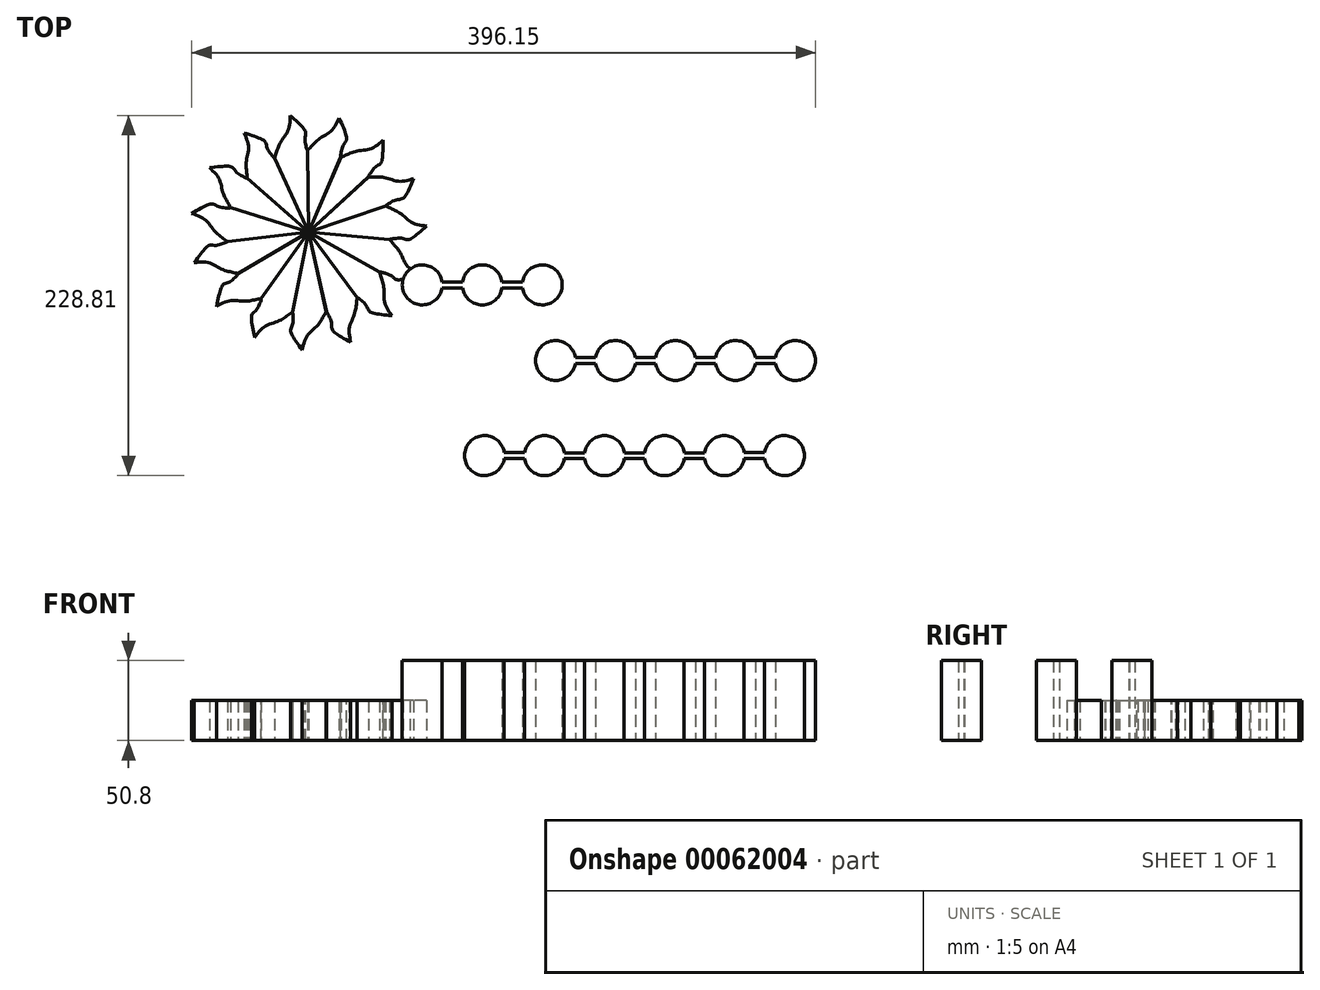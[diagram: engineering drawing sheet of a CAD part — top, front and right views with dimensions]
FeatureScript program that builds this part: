
annotation { "Feature Type Name" : "Feature", "Feature Type Description" : "" }
export const myFeature = defineFeature(function(context is Context, id is Id, definition is map)
    precondition{}
    {
        {
            var Q0;
            Q0=qCreatedBy(makeId("Top.planeOp"),FACE);
            var sketch = newSketch(context, id + "F0", { "sketchPlane" : qUnion([Q0])});
            skCircle(sketch, "E0", {"center": v(-72.3, 33.55) * mm, "radius": 46.86 * mm, "construction": true});
            skPoint(sketch, "E1", {"position": v(-84, 107.69) * mm});
            skPoint(sketch, "E2", {"position": v(-52.55, 106.29) * mm});
            skFitSpline(sketch, "E3", {"points": [v(-84, 107.69) * mm, v(-85.17, 98.25) * mm, v(-89.63, 91.3) * mm, v(-92.12, 85.8) * mm, v(-93.88, 80.61) * mm], "startDerivative": vector(-0.18, -34.68) * mm, "endDerivative": vector(-7.94, -23.8) * mm});
            skFitSpline(sketch, "E4", {"points": [v(-84, 107.69) * mm, v(-76.24, 100.43) * mm, v(-74.06, 96.7) * mm, v(-74.58, 92.65) * mm, v(-73.75, 87.67) * mm, v(-72.87, 85.38) * mm], "startDerivative": vector(30.23, -26.75) * mm, "endDerivative": vector(11.37, -13.18) * mm});
            skLineSegment(sketch, "E5", {"start": v(-93.88, 80.61) * mm, "end": v(-72.3, 33.55) * mm});
            skLineSegment(sketch, "E6", {"start": v(-72.87, 85.38) * mm, "end": v(-72.3, 33.55) * mm});
            skFitSpline(sketch, "E7", {"points": [v(64.47, 13.1) * mm, v(67.63, 14.05) * mm, v(71.16, 16.5) * mm, v(74.15, 19.89) * mm, v(77.5, 21.96) * mm, v(81.01, 21.97) * mm, v(84.14, 19.15) * mm, v(86.86, 16.13) * mm, v(90.86, 13.32) * mm, v(96.34, 13.11) * mm, v(100.52, 15.65) * mm, v(104.5, 20.68) * mm, v(107.3, 22) * mm, v(110.25, 22) * mm, v(114.68, 20.13) * mm, v(117.22, 16.95) * mm, v(119.43, 14.56) * mm, v(123.54, 13.1) * mm, v(127.31, 13.48) * mm, v(130.94, 16.58) * mm, v(133.75, 20.53) * mm, v(137.67, 22.62) * mm, v(142.59, 22.5) * mm, v(146.88, 19.99) * mm, v(149.63, 15.48) * mm, v(152.68, 13.12) * mm, v(156.88, 14.14) * mm, v(159.57, 16.3) * mm, v(162.65, 19.41) * mm, v(165.82, 22.33) * mm, v(169.52, 22.8) * mm, v(173.03, 21.96) * mm, v(176.07, 19.15) * mm, v(178.82, 16.33) * mm, v(181.12, 14.17) * mm, v(184.17, 13.82) * mm], "startDerivative": vector(117.4, 52.72) * mm, "endDerivative": vector(132.17, 7.88) * mm});
            skFitSpline(sketch, "E8", {"points": [v(64.19, 4.2) * mm, v(67.53, 4.68) * mm, v(69.9, 6.47) * mm, v(72.66, 9.33) * mm, v(75.17, 11.93) * mm, v(78.06, 13.73) * mm, v(80.35, 13.4) * mm, v(83.09, 12.14) * mm, v(85.56, 10.55) * mm, v(87.44, 8.03) * mm, v(89.85, 6.04) * mm, v(93.64, 5.11) * mm, v(98.68, 5.92) * mm, v(101.25, 8.04) * mm, v(102.63, 9.24) * mm, v(104.6, 11.3) * mm, v(106.71, 12.7) * mm, v(108.68, 13.7) * mm, v(112.02, 13.3) * mm, v(115.73, 10.79) * mm, v(117.15, 8.6) * mm, v(119.17, 7) * mm, v(121.72, 6.28) * mm, v(122.83, 6.15) * mm, v(129.57, 7.02) * mm, v(131.22, 8.02) * mm, v(132.93, 9.55) * mm, v(135.09, 12.5) * mm, v(137.14, 14.7) * mm, v(139.02, 15.83) * mm, v(140.48, 15.89) * mm, v(141.4, 15.34) * mm, v(143.75, 13.68) * mm, v(144.92, 12.42) * mm, v(146.1, 11.23) * mm, v(147.13, 10.17) * mm, v(149.73, 8.11) * mm, v(153.78, 7.12) * mm, v(156.8, 7.4) * mm, v(158.96, 8) * mm, v(160.87, 9.39) * mm, v(162.84, 10.52) * mm, v(163.63, 11.19) * mm, v(165.2, 12.78) * mm, v(166.8, 14.84) * mm, v(167.92, 16.44) * mm, v(171.06, 16.58) * mm, v(172.23, 15.06) * mm, v(174.04, 12.4) * mm, v(175.08, 11.2) * mm, v(176.31, 9.68) * mm, v(177.22, 8.61) * mm, v(178.07, 8.08) * mm, v(179.24, 7.16) * mm, v(180.74, 6.5) * mm, v(181.2, 6.43) * mm, v(182.37, 6.1) * mm, v(182.83, 6.03) * mm, v(183.74, 5.77) * mm], "startDerivative": vector(174.25, 6.05) * mm, "endDerivative": vector(94.47, -30.78) * mm});
            skLineSegment(sketch, "E9", {"start": v(64.47, 13.1) * mm, "end": v(64.19, 4.2) * mm});
            skLineSegment(sketch, "E10", {"start": v(184.17, 13.82) * mm, "end": v(203.03, 13.82) * mm});
            skLineSegment(sketch, "E11", {"start": v(183.74, 5.77) * mm, "end": v(203.06, 5.77) * mm});
            skLineSegment(sketch, "E12", {"start": v(203.06, 5.77) * mm, "end": v(203.06, 2.55) * mm});
            skLineSegment(sketch, "E13", {"start": v(203.06, 2.55) * mm, "end": v(212.9, 9.32) * mm});
            skLineSegment(sketch, "E14", {"start": v(212.9, 9.32) * mm, "end": v(203.05, 17.48) * mm});
            skLineSegment(sketch, "E15", {"start": v(203.05, 17.48) * mm, "end": v(203.03, 13.82) * mm});
            skSolve(sketch);
        }
        {
            var Q0;
            Q0=makeQuery(id+"F0.imprint","IMPRINT",FACE,{"disambiguationData":[TD([[makeQuery(id+"F0.imprint","IMPRINT",EDGE,{"derivedFrom":sQuery(id+"F0.wireOp",EDGE,"E3")}),1.0]])]});
            extrude(context, id + "F1", {"entities" : qUnion([Q0]), "depth" : 25.4 * mm});
        }
        {
            var Q0;
            Q0=makeQuery(id+"F1.opExtrude","SWEPT_BODY",BODY,{"disambiguationData":[OSD([sQuery(id+"F0.wireOp",EDGE,"E3"),sQuery(id+"F0.wireOp",EDGE,"E4"),sQuery(id+"F0.wireOp",EDGE,"E5"),sQuery(id+"F0.wireOp",EDGE,"E6")])]});
            var Q1;
            Q1=makeQuery(id+"F1.opExtrude","SWEPT_EDGE",EDGE,{"disambiguationData":[OSD([sQuery(id+"F0.wireOp",EDGE,"E5"),sQuery(id+"F0.wireOp",EDGE,"E6")])]});
            circularPattern(context, id + "F2", {"entities" : qUnion([Q0]), "axis" : qUnion([Q1]), "angle" : 24 * degree, "instanceCount" : 15});
        }
        {
            var Q0;
            Q0=qCreatedBy(makeId("Top.planeOp"),FACE);
            var sketch = newSketch(context, id + "F3", { "sketchPlane" : qUnion([Q0])});
            skArc(sketch, "E16", {"start": v(12.56, 1.9) * mm, "mid": v(-12.7, 0) * mm, "end": v(12.56, -1.9) * mm});
            skArc(sketch, "E17", {"start": v(25.55, -1.92) * mm, "mid": v(38.19, -12.7) * mm, "end": v(50.68, -1.74) * mm});
            skArc(sketch, "E18", {"start": v(63.65, -1.92) * mm, "mid": v(88.9, 0.09) * mm, "end": v(63.62, 1.74) * mm});
            skLineSegment(sketch, "E19", {"start": v(0, 0) * mm, "end": v(38.1, 0) * mm, "construction": true});
            skLineSegment(sketch, "E20", {"start": v(38.1, 0) * mm, "end": v(76.2, 0) * mm, "construction": true});
            skLineSegment(sketch, "E21.bottom", {"start": v(12.56, 1.9) * mm, "end": v(25.55, 1.9) * mm});
            skLineSegment(sketch, "E21.top", {"start": v(12.56, -1.92) * mm, "end": v(25.55, -1.92) * mm});
            skLineSegment(sketch, "E21.left", {"start": v(12.56, -1.9) * mm, "end": v(12.56, -1.92) * mm});
            skLineSegment(sketch, "E22.bottom", {"start": v(50.68, 1.74) * mm, "end": v(63.65, 1.74) * mm});
            skLineSegment(sketch, "E22.top", {"start": v(50.68, -1.92) * mm, "end": v(63.65, -1.92) * mm});
            skLineSegment(sketch, "E22.left", {"start": v(50.68, -1.74) * mm, "end": v(50.68, -1.92) * mm});
            skArc(sketch, "E23", {"start": v(97.19, -46.12) * mm, "mid": v(71.93, -48.02) * mm, "end": v(97.19, -49.93) * mm});
            skArc(sketch, "E24", {"start": v(135.31, -46.28) * mm, "mid": v(122.81, -35.32) * mm, "end": v(110.17, -46.12) * mm});
            skArc(sketch, "E25", {"start": v(148.28, -49.94) * mm, "mid": v(160.83, -60.72) * mm, "end": v(173.38, -49.94) * mm});
            skLineSegment(sketch, "E26", {"start": v(84.63, -48.02) * mm, "end": v(122.73, -48.02) * mm, "construction": true});
            skLineSegment(sketch, "E27", {"start": v(122.73, -48.02) * mm, "end": v(160.83, -48.02) * mm, "construction": true});
            skLineSegment(sketch, "E28.bottom", {"start": v(97.19, -46.12) * mm, "end": v(110.18, -46.12) * mm});
            skLineSegment(sketch, "E28.top", {"start": v(97.19, -49.94) * mm, "end": v(110.18, -49.94) * mm});
            skLineSegment(sketch, "E29.bottom", {"start": v(135.31, -46.28) * mm, "end": v(148.28, -46.28) * mm});
            skLineSegment(sketch, "E29.top", {"start": v(135.28, -49.94) * mm, "end": v(148.28, -49.94) * mm});
            skLineSegment(sketch, "E30", {"start": v(160.83, -38.76) * mm, "end": v(160.83, -58.68) * mm, "construction": true});
            skLineSegment(sketch, "E31.MirrorCS", {"start": v(224.47, -49.93) * mm, "end": v(224.47, -49.94) * mm});
            skArc(sketch, "E32.MirrorC", {"start": v(148.25, -46.28) * mm, "mid": v(160.83, -35.32) * mm, "end": v(173.41, -46.28) * mm});
            skArc(sketch, "E33.MirrorC", {"start": v(186.35, -46.28) * mm, "mid": v(198.85, -35.32) * mm, "end": v(211.49, -46.12) * mm});
            skLineSegment(sketch, "E34.MirrorCS", {"start": v(198.93, -48.02) * mm, "end": v(160.83, -48.02) * mm, "construction": true});
            skLineSegment(sketch, "E35.MirrorCS", {"start": v(224.47, -49.94) * mm, "end": v(211.48, -49.94) * mm});
            skArc(sketch, "E36.MirrorC", {"start": v(224.47, -46.12) * mm, "mid": v(249.73, -48.02) * mm, "end": v(224.47, -49.93) * mm});
            skLineSegment(sketch, "E37.MirrorCS", {"start": v(224.47, -46.12) * mm, "end": v(211.48, -46.12) * mm});
            skLineSegment(sketch, "E38.MirrorCS", {"start": v(237.03, -48.02) * mm, "end": v(198.93, -48.02) * mm, "construction": true});
            skLineSegment(sketch, "E39.MirrorCS", {"start": v(186.38, -49.94) * mm, "end": v(173.38, -49.94) * mm});
            skLineSegment(sketch, "E40.MirrorCS", {"start": v(186.35, -46.28) * mm, "end": v(173.38, -46.28) * mm});
            skArc(sketch, "E41", {"start": v(52.07, -106.52) * mm, "mid": v(26.81, -108.42) * mm, "end": v(52.07, -110.32) * mm});
            skArc(sketch, "E42", {"start": v(65.06, -110.34) * mm, "mid": v(77.61, -121.12) * mm, "end": v(90.16, -110.34) * mm});
            skArc(sketch, "E43", {"start": v(103.16, -110.34) * mm, "mid": v(115.71, -121.12) * mm, "end": v(128.26, -110.34) * mm});
            skLineSegment(sketch, "E44", {"start": v(39.51, -108.42) * mm, "end": v(77.61, -108.42) * mm, "construction": true});
            skLineSegment(sketch, "E45", {"start": v(77.61, -108.42) * mm, "end": v(115.71, -108.42) * mm, "construction": true});
            skLineSegment(sketch, "E46.bottom", {"start": v(52.07, -106.52) * mm, "end": v(65.06, -106.52) * mm});
            skLineSegment(sketch, "E46.top", {"start": v(52.07, -110.34) * mm, "end": v(65.06, -110.34) * mm});
            skLineSegment(sketch, "E47.bottom", {"start": v(90.2, -106.68) * mm, "end": v(103.16, -106.68) * mm});
            skLineSegment(sketch, "E47.top", {"start": v(90.16, -110.34) * mm, "end": v(103.16, -110.34) * mm});
            skLineSegment(sketch, "E48", {"start": v(115.71, -108.42) * mm, "end": v(134.76, -108.42) * mm, "construction": true});
            skLineSegment(sketch, "E49", {"start": v(134.76, -108.42) * mm, "end": v(134.76, -90.26) * mm, "construction": true});
            skLineSegment(sketch, "E50", {"start": v(128.3, -106.68) * mm, "end": v(134.76, -106.68) * mm});
            skLineSegment(sketch, "E51", {"start": v(128.26, -110.34) * mm, "end": v(134.76, -110.34) * mm});
            skLineSegment(sketch, "E52.MirrorCS", {"start": v(217.45, -110.34) * mm, "end": v(204.46, -110.34) * mm});
            skLineSegment(sketch, "E53.MirrorCS", {"start": v(153.81, -108.42) * mm, "end": v(134.76, -108.42) * mm, "construction": true});
            skLineSegment(sketch, "E54.MirrorCS", {"start": v(191.91, -108.42) * mm, "end": v(153.81, -108.42) * mm, "construction": true});
            skLineSegment(sketch, "E55.MirrorCS", {"start": v(230.01, -108.42) * mm, "end": v(191.91, -108.42) * mm, "construction": true});
            skLineSegment(sketch, "E56.MirrorCS", {"start": v(217.45, -106.52) * mm, "end": v(204.46, -106.52) * mm});
            skArc(sketch, "E57.MirrorC", {"start": v(217.45, -106.52) * mm, "mid": v(242.71, -108.42) * mm, "end": v(217.45, -110.32) * mm});
            skLineSegment(sketch, "E58.MirrorCS", {"start": v(141.26, -110.34) * mm, "end": v(134.76, -110.34) * mm});
            skLineSegment(sketch, "E59.MirrorCS", {"start": v(141.23, -106.68) * mm, "end": v(134.76, -106.68) * mm});
            skArc(sketch, "E60.MirrorC", {"start": v(141.23, -106.68) * mm, "mid": v(153.81, -95.72) * mm, "end": v(166.4, -106.68) * mm});
            skLineSegment(sketch, "E61.MirrorCS", {"start": v(179.33, -106.68) * mm, "end": v(166.36, -106.68) * mm});
            skArc(sketch, "E62.MirrorC", {"start": v(179.33, -106.68) * mm, "mid": v(191.83, -95.72) * mm, "end": v(204.47, -106.52) * mm});
            skLineSegment(sketch, "E63.MirrorCS", {"start": v(179.36, -110.34) * mm, "end": v(166.36, -110.34) * mm});
            skArc(sketch, "E64.trimOffspring", {"start": v(50.68, 1.74) * mm, "mid": v(38.18, 12.7) * mm, "end": v(25.54, 1.9) * mm});
            skLineSegment(sketch, "E65.trimOffspring", {"start": v(97.19, -49.93) * mm, "end": v(97.19, -49.94) * mm});
            skArc(sketch, "E66.trimOffspring", {"start": v(110.18, -49.94) * mm, "mid": v(122.73, -60.72) * mm, "end": v(135.28, -49.94) * mm});
            skArc(sketch, "E67.trimOffspring", {"start": v(173.41, -46.28) * mm, "mid": v(160.83, -35.32) * mm, "end": v(148.25, -46.28) * mm});
            skArc(sketch, "E68.trimOffspring", {"start": v(173.38, -49.94) * mm, "mid": v(160.83, -60.72) * mm, "end": v(148.28, -49.94) * mm});
            skArc(sketch, "E69.trimOffspring", {"start": v(211.48, -49.94) * mm, "mid": v(198.93, -60.72) * mm, "end": v(186.38, -49.94) * mm});
            skLineSegment(sketch, "E70.trimOffspring", {"start": v(52.07, -110.32) * mm, "end": v(52.07, -110.34) * mm});
            skArc(sketch, "E71.trimOffspring", {"start": v(90.2, -106.68) * mm, "mid": v(77.7, -95.72) * mm, "end": v(65.05, -106.52) * mm});
            skArc(sketch, "E72.trimOffspring", {"start": v(128.3, -106.68) * mm, "mid": v(115.71, -95.72) * mm, "end": v(103.13, -106.68) * mm});
            skArc(sketch, "E73.trimOffspring", {"start": v(166.36, -110.34) * mm, "mid": v(153.81, -121.12) * mm, "end": v(141.26, -110.34) * mm});
            skLineSegment(sketch, "E74.trimOffspring", {"start": v(217.45, -110.32) * mm, "end": v(217.45, -110.34) * mm});
            skArc(sketch, "E75.trimOffspring", {"start": v(204.46, -110.34) * mm, "mid": v(191.91, -121.12) * mm, "end": v(179.36, -110.34) * mm});
            skSolve(sketch);
        }
        {
            var Q0;
            {var subQ1=sQuery(id+"F3.wireOp",EDGE,"E16");Q0=makeQuery(id+"F3.imprint","IMPRINT",FACE,{"disambiguationData":[TD([[makeQuery(id+"F3.imprint","IMPRINT",EDGE,{"derivedFrom":subQ1}),1.0]])]});}
            var Q1;
            {var subQ5=sQuery(id+"F3.wireOp",EDGE,"E23");Q1=makeQuery(id+"F3.imprint","IMPRINT",FACE,{"disambiguationData":[TD([[makeQuery(id+"F3.imprint","IMPRINT",EDGE,{"derivedFrom":subQ5}),1.0]])]});}
            var Q2;
            {var subQ8=sQuery(id+"F3.wireOp",EDGE,"E41");Q2=makeQuery(id+"F3.imprint","IMPRINT",FACE,{"disambiguationData":[TD([[makeQuery(id+"F3.imprint","IMPRINT",EDGE,{"derivedFrom":subQ8}),1.0]])]});}
            extrude(context, id + "F4", {"entities" : qUnion([Q0, Q1, Q2]), "operationType" : NewBodyOperationType.ADD, "depth" : 50.8 * mm});
        }
    });
